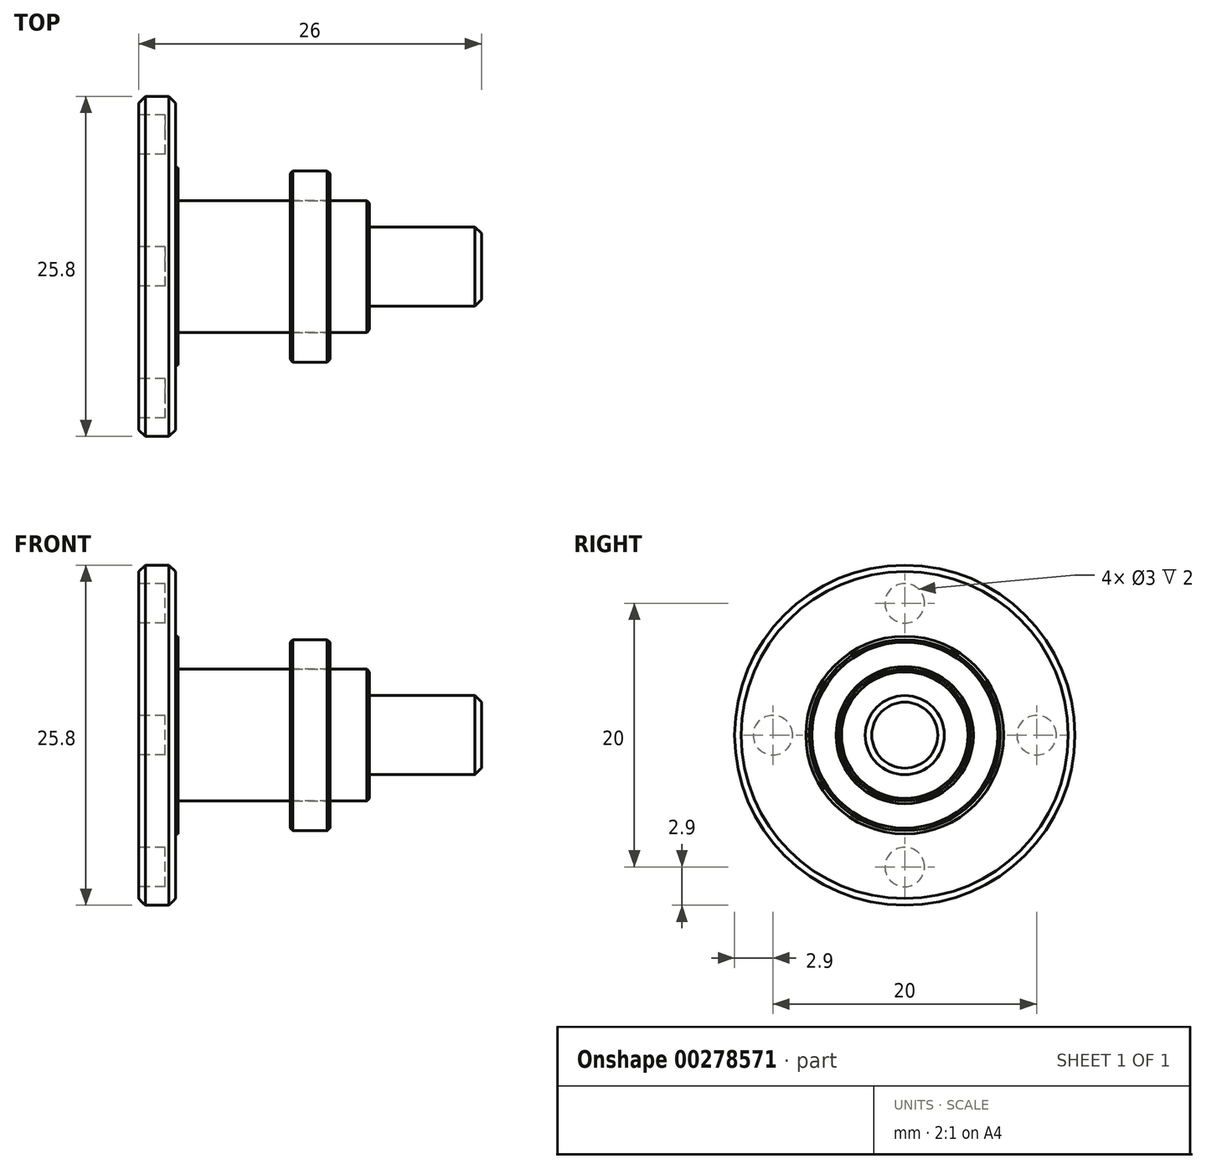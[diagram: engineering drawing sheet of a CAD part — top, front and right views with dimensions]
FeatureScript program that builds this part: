
annotation { "Feature Type Name" : "Feature", "Feature Type Description" : "" }
export const myFeature = defineFeature(function(context is Context, id is Id, definition is map)
    precondition{}
    {
        {
            var Q0;
            Q0=qCreatedBy(makeId("Right.planeOp"),FACE);
            var sketch = newSketch(context, id + "F0", { "sketchPlane" : qUnion([Q0])});
            skCircle(sketch, "E0", {"center": v(0, 0) * mm, "radius": 3 * mm});
            skCircle(sketch, "E1", {"center": v(0, 0) * mm, "radius": 7.5 * mm});
            skCircle(sketch, "E2", {"center": v(0, 0) * mm, "radius": 12.9 * mm});
            skCircle(sketch, "E3", {"center": v(0, 0) * mm, "radius": 5 * mm});
            skCircle(sketch, "E4", {"center": v(10, 0) * mm, "radius": 1.5 * mm});
            skCircle(sketch, "E5.1.0", {"center": v(0, 10) * mm, "radius": 1.5 * mm});
            skCircle(sketch, "E5.2.0", {"center": v(-10, 0) * mm, "radius": 1.5 * mm});
            skCircle(sketch, "E5.3.0", {"center": v(0, -10) * mm, "radius": 1.5 * mm});
            skSolve(sketch);
        }
        {
            var Q0;
            Q0=makeQuery(id+"F0.imprint","IMPRINT",FACE,{"disambiguationData":[TD([[makeQuery(id+"F0.imprint","IMPRINT",EDGE,{"derivedFrom":sQuery(id+"F0.wireOp",EDGE,"E0")}),1.0]])]});
            var Q1;
            Q1=makeQuery(id+"F0.imprint","IMPRINT",FACE,{"disambiguationData":[TD([[makeQuery(id+"F0.imprint","IMPRINT",EDGE,{"derivedFrom":sQuery(id+"F0.wireOp",EDGE,"E0")}),-1.0]])]});
            var Q2;
            Q2=makeQuery(id+"F0.imprint","IMPRINT",FACE,{"disambiguationData":[TD([[makeQuery(id+"F0.imprint","IMPRINT",EDGE,{"derivedFrom":sQuery(id+"F0.wireOp",EDGE,"E1")}),1.0]])]});
            var Q3;
            Q3=makeQuery(id+"F0.imprint","IMPRINT",FACE,{"disambiguationData":[TD([[makeQuery(id+"F0.imprint","IMPRINT",EDGE,{"derivedFrom":sQuery(id+"F0.wireOp",EDGE,"E1")}),-1.0]])]});
            var Q4;
            Q4=makeQuery(id+"F0.imprint","IMPRINT",FACE,{"disambiguationData":[TD([[makeQuery(id+"F0.imprint","IMPRINT",EDGE,{"derivedFrom":sQuery(id+"F0.wireOp",EDGE,"E4")}),1.0]])]});
            var Q5;
            Q5=makeQuery(id+"F0.imprint","IMPRINT",FACE,{"disambiguationData":[TD([[makeQuery(id+"F0.imprint","IMPRINT",EDGE,{"derivedFrom":sQuery(id+"F0.wireOp",EDGE,"E5.1.0")}),1.0]])]});
            var Q6;
            Q6=makeQuery(id+"F0.imprint","IMPRINT",FACE,{"disambiguationData":[TD([[makeQuery(id+"F0.imprint","IMPRINT",EDGE,{"derivedFrom":sQuery(id+"F0.wireOp",EDGE,"E5.2.0")}),1.0]])]});
            var Q7;
            Q7=makeQuery(id+"F0.imprint","IMPRINT",FACE,{"disambiguationData":[TD([[makeQuery(id+"F0.imprint","IMPRINT",EDGE,{"derivedFrom":sQuery(id+"F0.wireOp",EDGE,"E5.3.0")}),1.0]])]});
            extrude(context, id + "F1", {"entities" : qUnion([Q0, Q1, Q2, Q3, Q4, Q5, Q6, Q7]), "depth" : 2.8 * mm});
        }
        {
            var Q0;
            Q0=makeQuery(id+"F0.imprint","IMPRINT",FACE,{"disambiguationData":[TD([[makeQuery(id+"F0.imprint","IMPRINT",EDGE,{"derivedFrom":sQuery(id+"F0.wireOp",EDGE,"E0")}),1.0]])]});
            var Q1;
            Q1=makeQuery(id+"F0.imprint","IMPRINT",FACE,{"disambiguationData":[TD([[makeQuery(id+"F0.imprint","IMPRINT",EDGE,{"derivedFrom":sQuery(id+"F0.wireOp",EDGE,"E0")}),-1.0]])]});
            var Q2;
            Q2=makeQuery(id+"F0.imprint","IMPRINT",FACE,{"disambiguationData":[TD([[makeQuery(id+"F0.imprint","IMPRINT",EDGE,{"derivedFrom":sQuery(id+"F0.wireOp",EDGE,"E1")}),1.0]])]});
            extrude(context, id + "F2", {"entities" : qUnion([Q0, Q1, Q2]), "operationType" : NewBodyOperationType.ADD, "depth" : 3 * mm});
        }
        {
            var Q0;
            Q0=makeQuery(id+"F0.imprint","IMPRINT",FACE,{"disambiguationData":[TD([[makeQuery(id+"F0.imprint","IMPRINT",EDGE,{"derivedFrom":sQuery(id+"F0.wireOp",EDGE,"E0")}),1.0]])]});
            extrude(context, id + "F3", {"entities" : qUnion([Q0]), "operationType" : NewBodyOperationType.ADD, "depth" : 26 * mm});
        }
        {
            var Q0;
            Q0=makeQuery(id+"F1.opExtrude","CAP_EDGE",EDGE,{"disambiguationData":[OSD([sQuery(id+"F0.wireOp",EDGE,"E2")])],"isStart":true});
            var Q1;
            Q1=makeQuery(id+"F1.opExtrude","CAP_EDGE",EDGE,{"disambiguationData":[OSD([sQuery(id+"F0.wireOp",EDGE,"E2")])],"isStart":false});
            var Q2;
            Q2=makeQuery(id+"F3.opExtrude","CAP_EDGE",EDGE,{"disambiguationData":[OSD([sQuery(id+"F0.wireOp",EDGE,"E0")])],"isStart":false});
            chamfer(context, id + "F4", {"entities" : qUnion([Q0, Q1, Q2]), "width" : 0.5 * mm, "tangentPropagation" : true});
        }
        {
            var Q0;
            Q0=makeQuery(id+"F0.imprint","IMPRINT",FACE,{"disambiguationData":[TD([[makeQuery(id+"F0.imprint","IMPRINT",EDGE,{"derivedFrom":sQuery(id+"F0.wireOp",EDGE,"E0")}),1.0]])]});
            var Q1;
            Q1=makeQuery(id+"F0.imprint","IMPRINT",FACE,{"disambiguationData":[TD([[makeQuery(id+"F0.imprint","IMPRINT",EDGE,{"derivedFrom":sQuery(id+"F0.wireOp",EDGE,"E0")}),-1.0]])]});
            extrude(context, id + "F5", {"entities" : qUnion([Q0, Q1]), "operationType" : NewBodyOperationType.ADD, "depth" : 17.5 * mm});
        }
        {
            var Q0;
            Q0=makeQuery(id+"F0.imprint","IMPRINT",FACE,{"disambiguationData":[TD([[makeQuery(id+"F0.imprint","IMPRINT",EDGE,{"derivedFrom":sQuery(id+"F0.wireOp",EDGE,"E4")}),1.0]])]});
            var Q1;
            Q1=makeQuery(id+"F0.imprint","IMPRINT",FACE,{"disambiguationData":[TD([[makeQuery(id+"F0.imprint","IMPRINT",EDGE,{"derivedFrom":sQuery(id+"F0.wireOp",EDGE,"E5.3.0")}),1.0]])]});
            var Q2;
            Q2=makeQuery(id+"F0.imprint","IMPRINT",FACE,{"disambiguationData":[TD([[makeQuery(id+"F0.imprint","IMPRINT",EDGE,{"derivedFrom":sQuery(id+"F0.wireOp",EDGE,"E5.1.0")}),1.0]])]});
            var Q3;
            Q3=makeQuery(id+"F0.imprint","IMPRINT",FACE,{"disambiguationData":[TD([[makeQuery(id+"F0.imprint","IMPRINT",EDGE,{"derivedFrom":sQuery(id+"F0.wireOp",EDGE,"E5.2.0")}),1.0]])]});
            extrude(context, id + "F6", {"entities" : qUnion([Q0, Q1, Q2, Q3]), "operationType" : NewBodyOperationType.REMOVE, "depth" : 2 * mm});
        }
        {
            var Q0;
            Q0=makeQuery(id+"F6.boolean.opBoolean","COPY",EDGE,{"derivedFrom":makeQuery(id+"F6.opExtrude","CAP_EDGE",EDGE,{"disambiguationData":[OSD([sQuery(id+"F0.wireOp",EDGE,"E5.3.0")])],"isStart":true})});
            var Q1;
            Q1=makeQuery(id+"F6.boolean.opBoolean","COPY",EDGE,{"derivedFrom":makeQuery(id+"F6.opExtrude","CAP_EDGE",EDGE,{"disambiguationData":[OSD([sQuery(id+"F0.wireOp",EDGE,"E5.2.0")])],"isStart":true})});
            var Q2;
            Q2=makeQuery(id+"F6.boolean.opBoolean","COPY",EDGE,{"derivedFrom":makeQuery(id+"F6.opExtrude","CAP_EDGE",EDGE,{"disambiguationData":[OSD([sQuery(id+"F0.wireOp",EDGE,"E5.1.0")])],"isStart":true})});
            var Q3;
            Q3=makeQuery(id+"F6.boolean.opBoolean","COPY",EDGE,{"derivedFrom":makeQuery(id+"F6.opExtrude","CAP_EDGE",EDGE,{"disambiguationData":[OSD([sQuery(id+"F0.wireOp",EDGE,"E4")])],"isStart":true})});
            var Q4;
            Q4=makeQuery(id+"F5.opExtrude","CAP_EDGE",EDGE,{"disambiguationData":[OSD([sQuery(id+"F0.wireOp",EDGE,"E3")])],"isStart":false});
            chamfer(context, id + "F7", {"entities" : qUnion([Q0, Q1, Q2, Q3, Q4]), "width" : .2 * mm, "tangentPropagation" : true});
        }
        {
            var Q0;
            Q0=makeQuery(id+"F5.opExtrude","CAP_FACE",FACE,{"disambiguationData":[OSD([sQuery(id+"F0.wireOp",EDGE,"E3")])],"isStart":false});
            var sketch = newSketch(context, id + "F8", { "sketchPlane" : qUnion([Q0])});
            skCircle(sketch, "E6", {"center": v(0, 0) * mm, "radius": 5 * mm});
            skCircle(sketch, "E7", {"center": v(0, 0) * mm, "radius": 7.25 * mm});
            skSolve(sketch);
        }
        {
            var Q0;
            Q0=makeQuery(id+"F8.imprint","IMPRINT",FACE,{"disambiguationData":[TD([[makeQuery(id+"F8.imprint","IMPRINT",EDGE,{"derivedFrom":sQuery(id+"F8.wireOp",EDGE,"E6")}),-1.0]])]});
            extrude(context, id + "F9", {"entities" : qUnion([Q0]), "depth" : -6 * mm, "hasSecondDirection" : true, "secondDirectionOppositeDirection" : true, "secondDirectionDepth" : 3 * mm});
        }
        {
            var Q0;
            Q0=makeQuery(id+"F9.opExtrude","CAP_EDGE",EDGE,{"disambiguationData":[OSD([sQuery(id+"F8.wireOp",EDGE,"E6")])],"isStart":true});
            var Q1;
            Q1=makeQuery(id+"F9.opExtrude","CAP_EDGE",EDGE,{"disambiguationData":[OSD([sQuery(id+"F8.wireOp",EDGE,"E7")])],"isStart":true});
            var Q2;
            Q2=makeQuery(id+"F9.opExtrude","CAP_EDGE",EDGE,{"disambiguationData":[OSD([sQuery(id+"F8.wireOp",EDGE,"E7")])],"isStart":false});
            var Q3;
            Q3=makeQuery(id+"F9.opExtrude","CAP_EDGE",EDGE,{"disambiguationData":[OSD([sQuery(id+"F8.wireOp",EDGE,"E6")])],"isStart":false});
            chamfer(context, id + "F10", {"entities" : qUnion([Q0, Q1, Q2, Q3]), "width" : 0.2 * mm, "tangentPropagation" : true});
        }
    });
